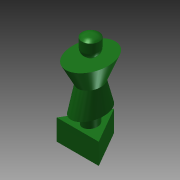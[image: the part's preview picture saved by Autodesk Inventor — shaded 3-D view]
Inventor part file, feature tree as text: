
AUTODESK INVENTOR PART (.ipt)
format: ipt  version: 2015 (Build 190159000, 159)  size: 235,008 bytes
history: native  units: in
note: dims shown in document units (in); Inventor stores cm internally (conversion verified against a paired STEP export)
features: sketch x8, plane x4, loft x3, extrude x1, revolve x1, projected_geometry x1, other x1
ambient origin geometry x8: Origin, YZ Plane, XZ Plane, XY Plane, X Axis, Y Axis, Z Axis, Center Point
bodies: Solid1 (feature_tree)
feature tree (19):
  extrude  "Extrusion1"  TaperAngle=0.0deg  [1 undecoded]
  sketch  "Sketch2"  dims[d5=0.32in d6=0.0in d8=0.105in]
  plane  "Work Plane1"
  loft  "Loft1"
  plane  "Work Plane2"
  sketch  "Sketch4"  dims[d11=0.11in d12=0.14in]
  loft  "Loft2"
  plane  "Work Plane3"
  loft  "Loft3"
  sketch  "Sketch8"  dims[d17=0.0in d18=90.0deg]
  plane  "Work Plane4"
  revolve  "Revolution1"  [1 undecoded]
  sketch  "Sketch1"  dims[d1=0.556in d3=0.0in]
  projected_geometry  "Projected Loop1"
  sketch  "Sketch3"  dims[d9=0.125in d10=0.19in]
  sketch  "Sketch5"  dims[d13=0.0in d14=0.0in]
  sketch  "Sketch7"  dims[d15=0.0in d16=90.0deg]
  other  "Edges1"
  sketch  "Sketch9"  dims[d19=0.36in d20=0.155in d21=0.195in d22=0.2in d23=0.3in d24=0.0in d25=90.0deg d26=0.0in d27=90.0deg d28=0.34in d29=0.27in d30=0.38in d31=0.0in d32=90.0deg d33=0.0in d34=90.0deg d35=90.0deg d36=90.0deg]
note: 2 required parameter values undecoded (feature->parameter linkage not recoverable at this tier; creation-order binding heuristic only, values carry confidence <= 0.55)